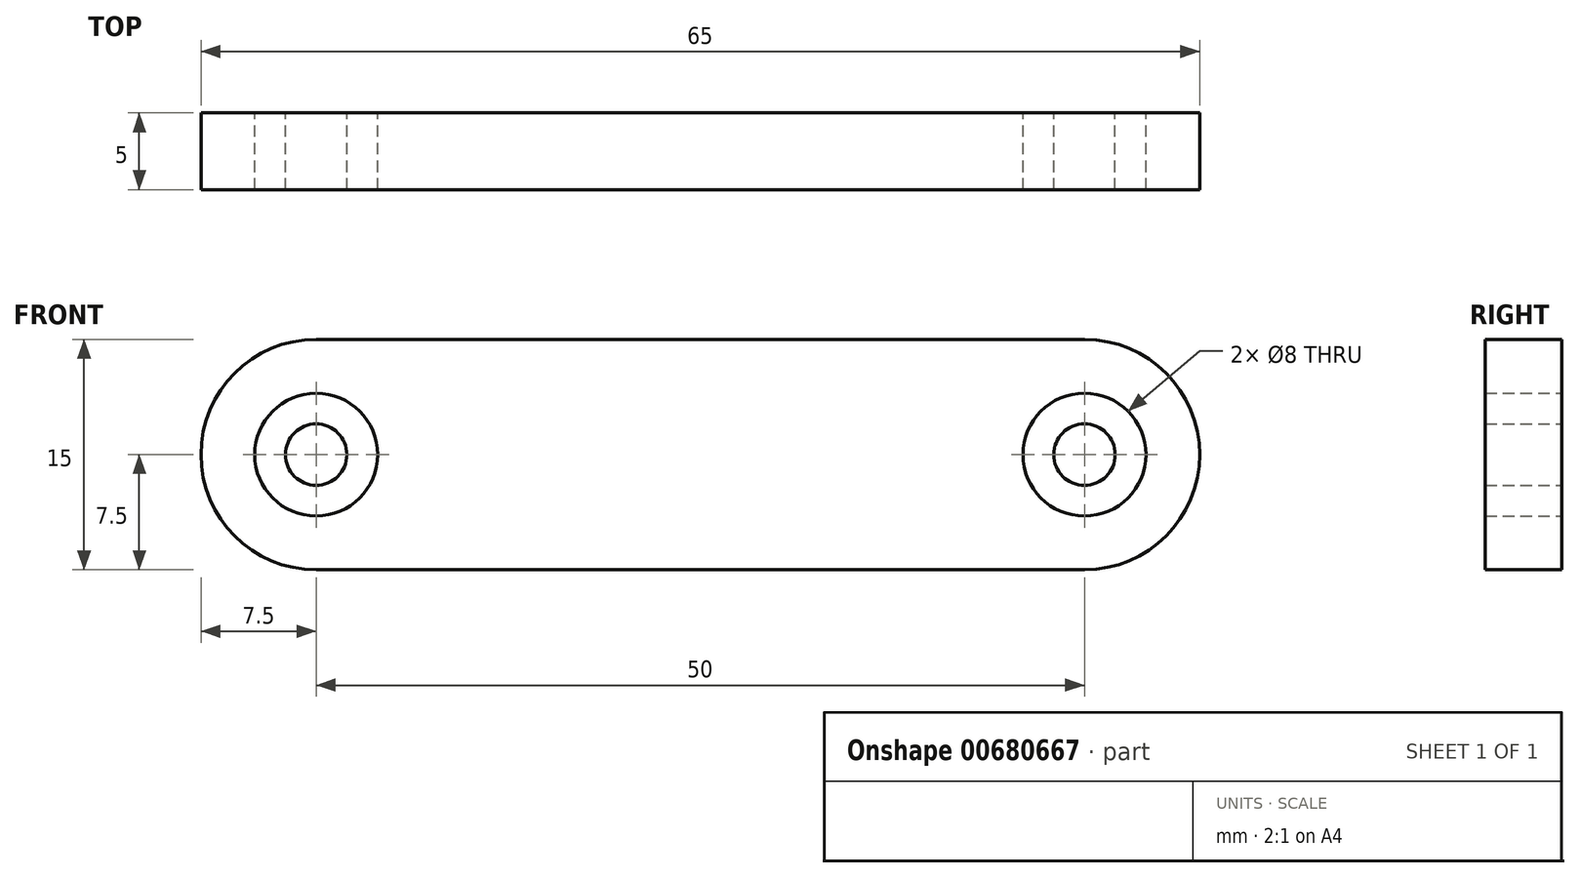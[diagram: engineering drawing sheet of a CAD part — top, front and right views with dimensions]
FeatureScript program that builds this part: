
annotation { "Feature Type Name" : "Feature", "Feature Type Description" : "" }
export const myFeature = defineFeature(function(context is Context, id is Id, definition is map)
    precondition{}
    {
        {
            var Q0;
            Q0=qCreatedBy(makeId("Front.planeOp"),FACE);
            var sketch = newSketch(context, id + "F0", { "sketchPlane" : qUnion([Q0])});
            skArc(sketch, "E0", {"start": v(0, 7.5) * mm, "mid": v(-7.5, 0) * mm, "end": v(0, -7.5) * mm});
            skArc(sketch, "E1", {"start": v(50, -7.5) * mm, "mid": v(57.5, 0) * mm, "end": v(50, 7.5) * mm});
            skCircle(sketch, "E2", {"center": v(0, 0) * mm, "radius": 2 * mm});
            skCircle(sketch, "E3", {"center": v(0, 0) * mm, "radius": 4 * mm});
            skCircle(sketch, "E4", {"center": v(50, 0) * mm, "radius": 4 * mm});
            skCircle(sketch, "E5", {"center": v(50, 0) * mm, "radius": 2 * mm});
            skLineSegment(sketch, "E6", {"start": v(0, 7.5) * mm, "end": v(50, 7.5) * mm});
            skLineSegment(sketch, "E7", {"start": v(0, -7.5) * mm, "end": v(50, -7.5) * mm});
            skSolve(sketch);
        }
        {
            var Q0;
            Q0=makeQuery(id+"F0.imprint","IMPRINT",FACE,{"disambiguationData":[TD([[makeQuery(id+"F0.imprint","IMPRINT",EDGE,{"derivedFrom":sQuery(id+"F0.wireOp",EDGE,"E2")}),1.0]])]});
            var Q1;
            Q1=makeQuery(id+"F0.imprint","IMPRINT",FACE,{"disambiguationData":[TD([[makeQuery(id+"F0.imprint","IMPRINT",EDGE,{"derivedFrom":sQuery(id+"F0.wireOp",EDGE,"E5")}),1.0]])]});
            var Q2;
            Q2=makeQuery(id+"F0.imprint","IMPRINT",FACE,{"disambiguationData":[TD([[makeQuery(id+"F0.imprint","IMPRINT",EDGE,{"derivedFrom":sQuery(id+"F0.wireOp",EDGE,"E0")}),1.0]])]});
            extrude(context, id + "F1", {"entities" : qUnion([Q0, Q1, Q2]), "depth" : 5 * mm, "offsetDistance" : 25.4 * mm});
        }
    });
